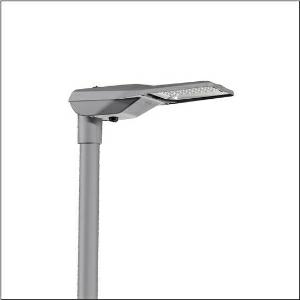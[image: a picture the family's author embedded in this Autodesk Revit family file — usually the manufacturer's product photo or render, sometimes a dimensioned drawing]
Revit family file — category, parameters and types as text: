
# Revit family: streetlight_sl_21_mini___st1_0a_5xe2d43t08hb_126b
name_source: partatom
category: Lighting Fixtures
units: mm (PartAtom-declared; Revit-internal decimal feet)

## family parameters
Cut with Voids When Loaded = No
Host = Face
Light Source = No
Part Type = Normal
Room Calculation Point = No
Round Connector Dimension = Use Diameter
Shared = No

## types (1)
- --- (1 x LED, 9430 lm, 66 W, 4000K)
    Apparent Load = 66 VA
    CIE Flux Codes = 37 72 97 100 100
    Color Rendering = 70
    Color Temperature = 4000K
    Default Elevation = 1800 mm
    Description = Streetlight SL 21 mini, mast luminaire, primary light control with lens, of PMMA, primary optical cover: cover, of toughened safety glass, transparent, light distribution: ST1.0a, light emission: direct distribution, primary light characteristic: asymmetric, installation type: side-entry, post-top, LED, High Power LED, rated luminous flux: 9.430lm, luminous efficacy: 143lm/W, light colour: 740, colour temperature: 4000K, control gear: D4i, control: overheat protection, constant luminous flux control, time-dependent luminous flux control, flexible luminous flux parameterisation, pre-setting: logarithmic dimming characteristic, mains connection: 220..240V, AC, 50/60Hz, start of lifetime: 66W, end of service life: 69W, reduction: 30W, luminaire housing, of diecast aluminium, powder-coated, SITECO metallic grey (DB 702S), corrosivity category C5 high according to DIN EN ISO 12944, please order mast flange separately, inclination adjustable: 0°, 5°, 10°, 15°, sealing non-destructively replaceable, multi-level sealing system, length: 628mm, width: 235mm, height: 110mm, mast flange for spigot size: 42mm (side-entry): 5XC10008XM4, 60/48mm (side-entry/post-top): 5XC10108XM2, 76/60mm (side-entry/post-top): 5XC10108XM1, mounting height: 4..8m, Smart Interface below and above, protection rating (complete): IP66, insulation class (complete): insulation class II (safety insulation), certification: CE, ENEC, ENEC+, VDE, impact resistance: IK10, permissible operating ambient temperature for outdoor applications: -40..+50°C, standard-compliant lighting for roads and squares, packaging unit: 1 piece

Light Distribution: ST1.0a
    Height = 110 mm
    Lamp = 1 x LED
    Lamp Light Flux = 9430 lm
    Lamp Power = 66 W
    Lamp count = 1
    Length = 625 mm
    Luminous efficacy = 143 lm/W
    Manufacturer = Siteco
    ModVariant = No
    Model = 5XE2D43T08HB
    Number of Poles = 1
    OnlyDefault = Yes
    Power Factor = 1
    Product Name = Streetlight SL 21 mini | ST1.0a
    Product group = mast luminaire | pylon top
    ProductGroupID = 6100
    Protection Class = Protection class II
    Protection Degree = IP 66
    RLX_Detail_Level = 1
    RLX_Emergency_Light_Flux = 0 lm
    RLX_Emergency_Type = 0
    RLX_Emergency_Type_DB = No
    RlxData = <blob elided: 26253 chars, md5=5bc7d500>
    Socket = socket
    Standby Power = 0 W
    System Light Flux = 9430 lm
    System Power = 66 W
    Type Comments = factory setting: luminous flux: 100 % | dim-lin: 254 | 670 mA
    Type Image = l_1003514.jpg
    URL = http://relux.com
    VarID = @adj_185899
    Voltage = 0 V
    Weight = 0.00 kg
    Width = 234 mm

## geometry (parser evidence)
native form markers: Blend x4, Sweep x13
no freeform markers — native parametric forms only
